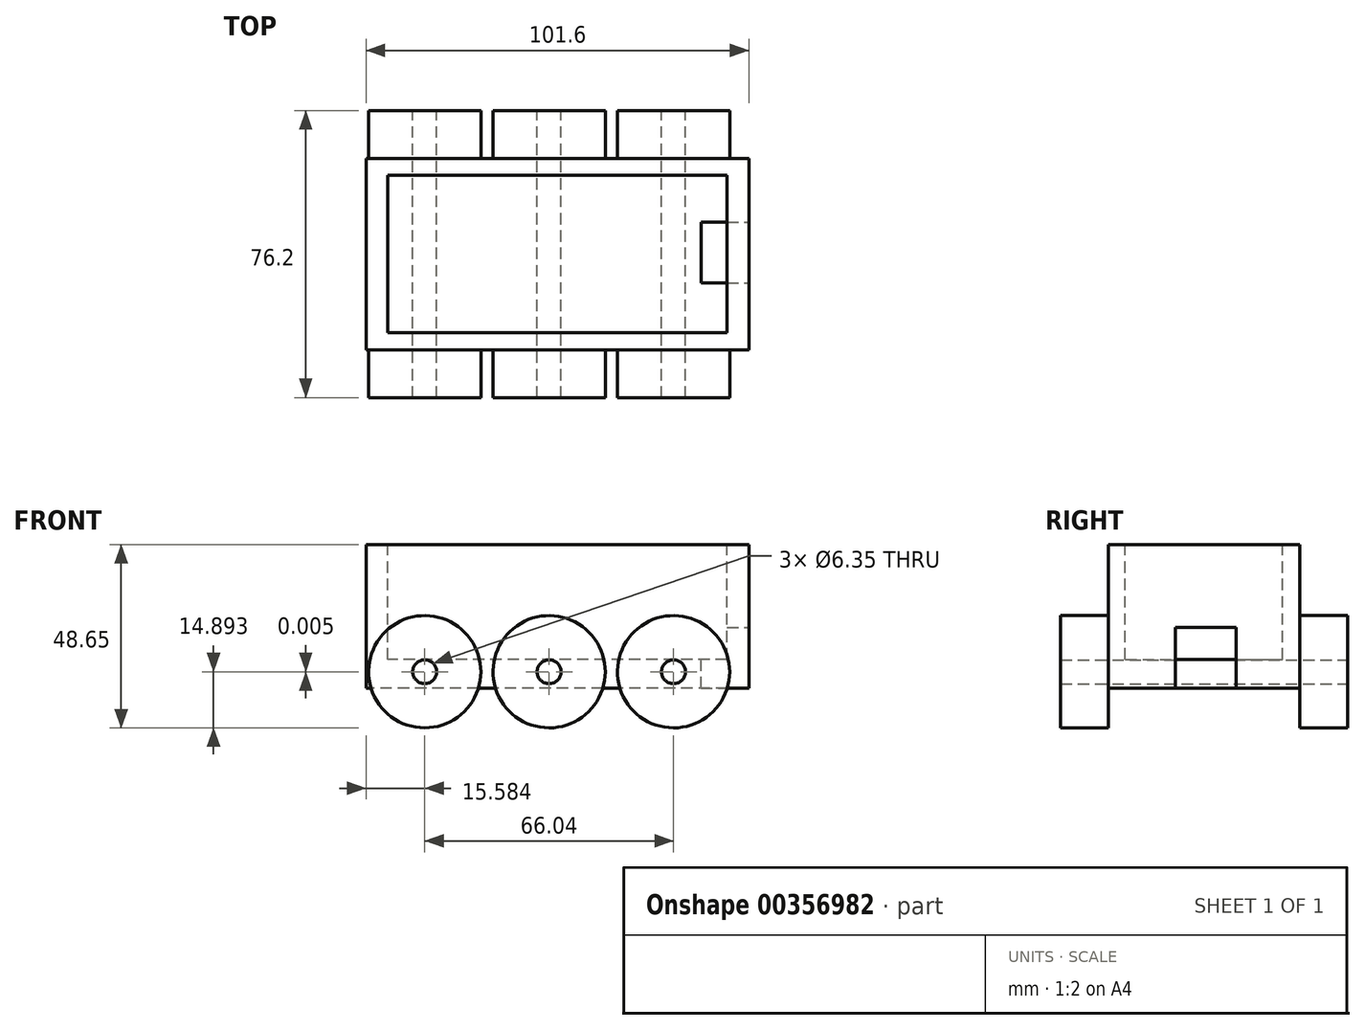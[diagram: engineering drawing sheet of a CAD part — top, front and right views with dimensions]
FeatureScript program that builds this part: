
annotation { "Feature Type Name" : "Feature", "Feature Type Description" : "" }
export const myFeature = defineFeature(function(context is Context, id is Id, definition is map)
    precondition{}
    {
        {
            var Q0;
            Q0=qCreatedBy(makeId("Front.planeOp"),FACE);
            var sketch = newSketch(context, id + "F0", { "sketchPlane" : qUnion([Q0])});
            skLineSegment(sketch, "E0.bottom", {"start": v(50.8, -19.05) * mm, "end": v(-50.8, -19.05) * mm});
            skLineSegment(sketch, "E0.top", {"start": v(50.8, 19.05) * mm, "end": v(-50.8, 19.05) * mm});
            skLineSegment(sketch, "E0.left", {"start": v(50.8, -19.05) * mm, "end": v(50.8, 19.05) * mm});
            skLineSegment(sketch, "E0.right", {"start": v(-50.8, -19.05) * mm, "end": v(-50.8, 19.05) * mm});
            skPoint(sketch, "E0.middle", {"position": v(0, 0) * mm});
            skLineSegment(sketch, "E1", {"start": v(50.8, 0) * mm, "end": v(92.45, 29.09) * mm});
            skLineSegment(sketch, "E2", {"start": v(50.8, -8.42) * mm, "end": v(97.5, 23.51) * mm});
            skCircle(sketch, "E3", {"center": v(94.98, 26.3) * mm, "radius": 3.76 * mm});
            skPoint(sketch, "E3.third.point", {"position": v(92.45, 23.51) * mm});
            skSolve(sketch);
        }
        {
            var Q0;
            {var subQ0=sQuery(id+"F0.wireOp",EDGE,"E3");var subQ1=sQuery(id+"F0.wireOp",EDGE,"E2");var subQ2=makeQuery(id+"F0.imprint","INTERSECT",VERTEX,{"disambiguationData":[OD(0.0)],"derivedFrom":[subQ1,subQ0]});Q0=makeQuery(id+"F0.imprint","IMPRINT",FACE,{"disambiguationData":[TD([[makeQuery(id+"F0.imprint","IMPRINT",EDGE,{"disambiguationData":[TD([[subQ2,1.0]])],"derivedFrom":subQ1}),-1.0]])]});}
            var Q1;
            {var subQ5=sQuery(id+"F0.wireOp",EDGE,"E0.top");Q1=makeQuery(id+"F0.imprint","IMPRINT",FACE,{"disambiguationData":[TD([[makeQuery(id+"F0.imprint","IMPRINT",EDGE,{"derivedFrom":subQ5}),1.0]])]});}
            var Q2;
            {var subQ0=sQuery(id+"F0.wireOp",EDGE,"3RzWjaEX-l5eM-vUkJ-IRTJ-Bg9MfRm08gdL");var subQ1=sQuery(id+"F0.wireOp",EDGE,"E0.bottom");var subQ2=makeQuery(id+"F0.imprint","INTERSECT",VERTEX,{"disambiguationData":[OD(0.0)],"derivedFrom":[subQ1,subQ0]});Q2=makeQuery(id+"F0.imprint","IMPRINT",FACE,{"disambiguationData":[TD([[makeQuery(id+"F0.imprint","IMPRINT",EDGE,{"disambiguationData":[TD([[subQ2,-1.0]])],"derivedFrom":subQ1}),-1.0]])]});}
            var Q3;
            {var subQ0=sQuery(id+"F0.wireOp",EDGE,"Zbk6lNHx-AOhV-0pgD-GcxR-QwvbEKfbeyAy");var subQ1=sQuery(id+"F0.wireOp",EDGE,"E0.bottom");var subQ2=makeQuery(id+"F0.imprint","INTERSECT",VERTEX,{"disambiguationData":[OD(0.0)],"derivedFrom":[subQ1,subQ0]});Q3=makeQuery(id+"F0.imprint","IMPRINT",FACE,{"disambiguationData":[TD([[makeQuery(id+"F0.imprint","IMPRINT",EDGE,{"disambiguationData":[TD([[subQ2,-1.0]])],"derivedFrom":subQ1}),-1.0]])]});}
            var Q4;
            {var subQ0=sQuery(id+"F0.wireOp",EDGE,"ppbOPpaH-TyTr-80lQ-VF5F-82fp93MNXJaD");var subQ1=sQuery(id+"F0.wireOp",EDGE,"E0.bottom");var subQ2=makeQuery(id+"F0.imprint","INTERSECT",VERTEX,{"disambiguationData":[OD(0.0)],"derivedFrom":[subQ1,subQ0]});Q4=makeQuery(id+"F0.imprint","IMPRINT",FACE,{"disambiguationData":[TD([[makeQuery(id+"F0.imprint","IMPRINT",EDGE,{"disambiguationData":[TD([[subQ2,-1.0]])],"derivedFrom":subQ1}),-1.0]])]});}
            extrude(context, id + "F1", {"entities" : qUnion([Q0, Q1, Q2, Q3, Q4]), "endBound" : BoundingType.SYMMETRIC, "depth" : 50.8 * mm});
        }
        {
            var Q0;
            Q0=makeQuery(id+"F1.opExtrude","CAP_FACE",FACE,{"disambiguationData":[OSD([sQuery(id+"F0.wireOp",EDGE,"E0.bottom"),sQuery(id+"F0.wireOp",EDGE,"E0.top"),sQuery(id+"F0.wireOp",EDGE,"E0.left"),sQuery(id+"F0.wireOp",EDGE,"E0.right")])],"isStart":false});
            var sketch = newSketch(context, id + "F2", { "sketchPlane" : qUnion([Q0])});
            skCircle(sketch, "E4", {"center": v(-35.22, -14.7) * mm, "radius": 14.9 * mm});
            skCircle(sketch, "E5", {"center": v(-2.2, -14.7) * mm, "radius": 14.9 * mm});
            skCircle(sketch, "E6", {"center": v(30.82, -14.7) * mm, "radius": 14.9 * mm});
            skCircle(sketch, "E7", {"center": v(-35.22, -14.7) * mm, "radius": 3.18 * mm});
            skCircle(sketch, "E8", {"center": v(-2.2, -14.7) * mm, "radius": 3.18 * mm});
            skCircle(sketch, "E9", {"center": v(30.82, -14.7) * mm, "radius": 3.18 * mm});
            skSolve(sketch);
        }
        {
            var Q0;
            {var subQ0=sQuery(id+"F2.wireOp",EDGE,"E6");var subQ1=makeQuery(id+"F1.opExtrude","CAP_EDGE",EDGE,{"disambiguationData":[OSD([sQuery(id+"F0.wireOp",EDGE,"E0.bottom")])],"isStart":false});var subQ2=makeQuery(id+"F2.imprint","INTERSECT",VERTEX,{"disambiguationData":[OD(0.0)],"derivedFrom":[subQ1,subQ0]});Q0=makeQuery(id+"F2.imprint","IMPRINT",FACE,{"disambiguationData":[TD([[makeQuery(id+"F2.imprint","IMPRINT",EDGE,{"disambiguationData":[TD([[subQ2,1.0]])],"derivedFrom":subQ0}),1.0]])]});}
            var Q1;
            Q1=makeQuery(id+"F2.imprint","IMPRINT",FACE,{"disambiguationData":[TD([[makeQuery(id+"F2.imprint","IMPRINT",EDGE,{"derivedFrom":sQuery(id+"F2.wireOp",EDGE,"E9")}),-1.0]])]});
            var Q2;
            Q2=makeQuery(id+"F2.imprint","IMPRINT",FACE,{"disambiguationData":[TD([[makeQuery(id+"F2.imprint","IMPRINT",EDGE,{"derivedFrom":sQuery(id+"F2.wireOp",EDGE,"E8")}),-1.0]])]});
            var Q3;
            {var subQ0=sQuery(id+"F2.wireOp",EDGE,"E5");var subQ1=makeQuery(id+"F1.opExtrude","CAP_EDGE",EDGE,{"disambiguationData":[OSD([sQuery(id+"F0.wireOp",EDGE,"E0.bottom")])],"isStart":false});var subQ2=makeQuery(id+"F2.imprint","INTERSECT",VERTEX,{"disambiguationData":[OD(0.0)],"derivedFrom":[subQ1,subQ0]});Q3=makeQuery(id+"F2.imprint","IMPRINT",FACE,{"disambiguationData":[TD([[makeQuery(id+"F2.imprint","IMPRINT",EDGE,{"disambiguationData":[TD([[subQ2,-1.0]])],"derivedFrom":subQ0}),1.0]])]});}
            var Q4;
            Q4=makeQuery(id+"F2.imprint","IMPRINT",FACE,{"disambiguationData":[TD([[makeQuery(id+"F2.imprint","IMPRINT",EDGE,{"derivedFrom":sQuery(id+"F2.wireOp",EDGE,"E7")}),-1.0]])]});
            var Q5;
            {var subQ0=sQuery(id+"F2.wireOp",EDGE,"E4");var subQ1=makeQuery(id+"F1.opExtrude","CAP_EDGE",EDGE,{"disambiguationData":[OSD([sQuery(id+"F0.wireOp",EDGE,"E0.bottom")])],"isStart":false});var subQ2=makeQuery(id+"F2.imprint","INTERSECT",VERTEX,{"disambiguationData":[OD(0.0)],"derivedFrom":[subQ1,subQ0]});Q5=makeQuery(id+"F2.imprint","IMPRINT",FACE,{"disambiguationData":[TD([[makeQuery(id+"F2.imprint","IMPRINT",EDGE,{"disambiguationData":[TD([[subQ2,-1.0]])],"derivedFrom":subQ0}),1.0]])]});}
            extrude(context, id + "F3", {"entities" : qUnion([Q0, Q1, Q2, Q3, Q4, Q5]), "depth" : 12.7 * mm});
        }
        {
            var Q0;
            Q0=makeQuery(id+"F3.opExtrude","SWEPT_BODY",BODY,{"disambiguationData":[OSD([sQuery(id+"F2.wireOp",EDGE,"E6"),sQuery(id+"F2.wireOp",EDGE,"E9")])]});
            var Q1;
            Q1=makeQuery(id+"F3.opExtrude","SWEPT_BODY",BODY,{"disambiguationData":[OSD([sQuery(id+"F2.wireOp",EDGE,"E5"),sQuery(id+"F2.wireOp",EDGE,"E8")])]});
            var Q2;
            Q2=makeQuery(id+"F3.opExtrude","SWEPT_BODY",BODY,{"disambiguationData":[OSD([sQuery(id+"F2.wireOp",EDGE,"E4"),sQuery(id+"F2.wireOp",EDGE,"E7")])]});
            var Q3;
            Q3=qCreatedBy(makeId("Front.planeOp"),FACE);
            mirror(context, id + "F4", {"operationType" : NewBodyOperationType.ADD, "entities" : qUnion([Q0, Q1, Q2]), "mirrorPlane" : qUnion([Q3])});
        }
        {
            var Q0;
            Q0=makeQuery(id+"F1.opExtrude","SWEPT_FACE",FACE,{"disambiguationData":[OSD([sQuery(id+"F0.wireOp",EDGE,"E0.top")])]});
            var sketch = newSketch(context, id + "F5", { "sketchPlane" : qUnion([Q0])});
            skLineSegment(sketch, "E10.bottom", {"start": v(45, -20.9) * mm, "end": v(-45, -20.9) * mm});
            skLineSegment(sketch, "E10.top", {"start": v(45, 20.9) * mm, "end": v(-45, 20.9) * mm});
            skLineSegment(sketch, "E10.left", {"start": v(45, -20.9) * mm, "end": v(45, 20.9) * mm});
            skLineSegment(sketch, "E10.right", {"start": v(-45, -20.9) * mm, "end": v(-45, 20.9) * mm});
            skPoint(sketch, "E10.middle", {"position": v(0, 0) * mm});
            skSolve(sketch);
        }
        {
            var Q0;
            Q0=makeQuery(id+"F5.imprint","IMPRINT",FACE,{"disambiguationData":[TD([[makeQuery(id+"F5.imprint","IMPRINT",EDGE,{"derivedFrom":sQuery(id+"F5.wireOp",EDGE,"E10.bottom")}),-1.0]])]});
            extrude(context, id + "F6", {"entities" : qUnion([Q0]), "operationType" : NewBodyOperationType.REMOVE, "oppositeDirection" : true, "depth" : 30.48 * mm});
        }
        {
            var Q0;
            Q0=makeQuery(id+"F1.opExtrude","SWEPT_FACE",FACE,{"disambiguationData":[OSD([sQuery(id+"F0.wireOp",EDGE,"E0.left")])]});
            var sketch = newSketch(context, id + "F7", { "sketchPlane" : qUnion([Q0])});
            skLineSegment(sketch, "E11.bottom", {"start": v(-7.62, -19.05) * mm, "end": v(8.5, -19.05) * mm});
            skLineSegment(sketch, "E11.top", {"start": v(-7.62, -2.93) * mm, "end": v(8.5, -2.93) * mm});
            skLineSegment(sketch, "E11.left", {"start": v(-7.62, -19.05) * mm, "end": v(-7.62, -2.93) * mm});
            skLineSegment(sketch, "E11.right", {"start": v(8.5, -19.05) * mm, "end": v(8.5, -2.93) * mm});
            skSolve(sketch);
        }
        {
            var Q0;
            Q0=makeQuery(id+"F7.imprint","IMPRINT",FACE,{"disambiguationData":[TD([[makeQuery(id+"F7.imprint","IMPRINT",EDGE,{"derivedFrom":sQuery(id+"F7.wireOp",EDGE,"E11.bottom")}),1.0]])]});
            extrude(context, id + "F8", {"entities" : qUnion([Q0]), "oppositeDirection" : true, "depth" : 12.7 * mm});
        }
        {
            var Q0;
            Q0=makeQuery(id+"F2.imprint","IMPRINT",FACE,{"disambiguationData":[TD([[makeQuery(id+"F2.imprint","IMPRINT",EDGE,{"derivedFrom":sQuery(id+"F2.wireOp",EDGE,"E7")}),1.0]])]});
            var Q1;
            Q1=makeQuery(id+"F2.imprint","IMPRINT",FACE,{"disambiguationData":[TD([[makeQuery(id+"F2.imprint","IMPRINT",EDGE,{"derivedFrom":sQuery(id+"F2.wireOp",EDGE,"E8")}),1.0]])]});
            var Q2;
            Q2=makeQuery(id+"F2.imprint","IMPRINT",FACE,{"disambiguationData":[TD([[makeQuery(id+"F2.imprint","IMPRINT",EDGE,{"derivedFrom":sQuery(id+"F2.wireOp",EDGE,"E9")}),1.0]])]});
            var Q3;
            Q3=sQuery(id+"F2.wireOp",EDGE,"E7");
            var Q4;
            Q4=sQuery(id+"F2.wireOp",EDGE,"E8");
            var Q5;
            Q5=sQuery(id+"F2.wireOp",EDGE,"E9");
            extrude(context, id + "F9", {"entities" : qUnion([Q0, Q1, Q2]), "operationType" : NewBodyOperationType.REMOVE, "surfaceEntities" : qUnion([Q3, Q4, Q5]), "oppositeDirection" : true, "depth" : 25.4 * mm});
        }
        {
            var Q0;
            Q0=makeQuery(id+"F2.imprint","IMPRINT",FACE,{"disambiguationData":[TD([[makeQuery(id+"F2.imprint","IMPRINT",EDGE,{"derivedFrom":sQuery(id+"F2.wireOp",EDGE,"E8")}),1.0]])]});
            var Q1;
            Q1=makeQuery(id+"F2.imprint","IMPRINT",FACE,{"disambiguationData":[TD([[makeQuery(id+"F2.imprint","IMPRINT",EDGE,{"derivedFrom":sQuery(id+"F2.wireOp",EDGE,"E7")}),1.0]])]});
            var Q2;
            Q2=makeQuery(id+"F2.imprint","IMPRINT",FACE,{"disambiguationData":[TD([[makeQuery(id+"F2.imprint","IMPRINT",EDGE,{"derivedFrom":sQuery(id+"F2.wireOp",EDGE,"E9")}),1.0]])]});
            extrude(context, id + "F10", {"entities" : qUnion([Q0, Q1, Q2]), "operationType" : NewBodyOperationType.REMOVE, "oppositeDirection" : true, "depth" : 101.6 * mm});
        }
        {
            var Q0;
            Q0=makeQuery(id+"F7.imprint","IMPRINT",FACE,{"disambiguationData":[TD([[makeQuery(id+"F7.imprint","IMPRINT",EDGE,{"derivedFrom":sQuery(id+"F7.wireOp",EDGE,"E11.bottom")}),1.0]])]});
            extrude(context, id + "F11", {"entities" : qUnion([Q0]), "operationType" : NewBodyOperationType.REMOVE, "oppositeDirection" : true, "depth" : 12.7 * mm});
        }
    });
